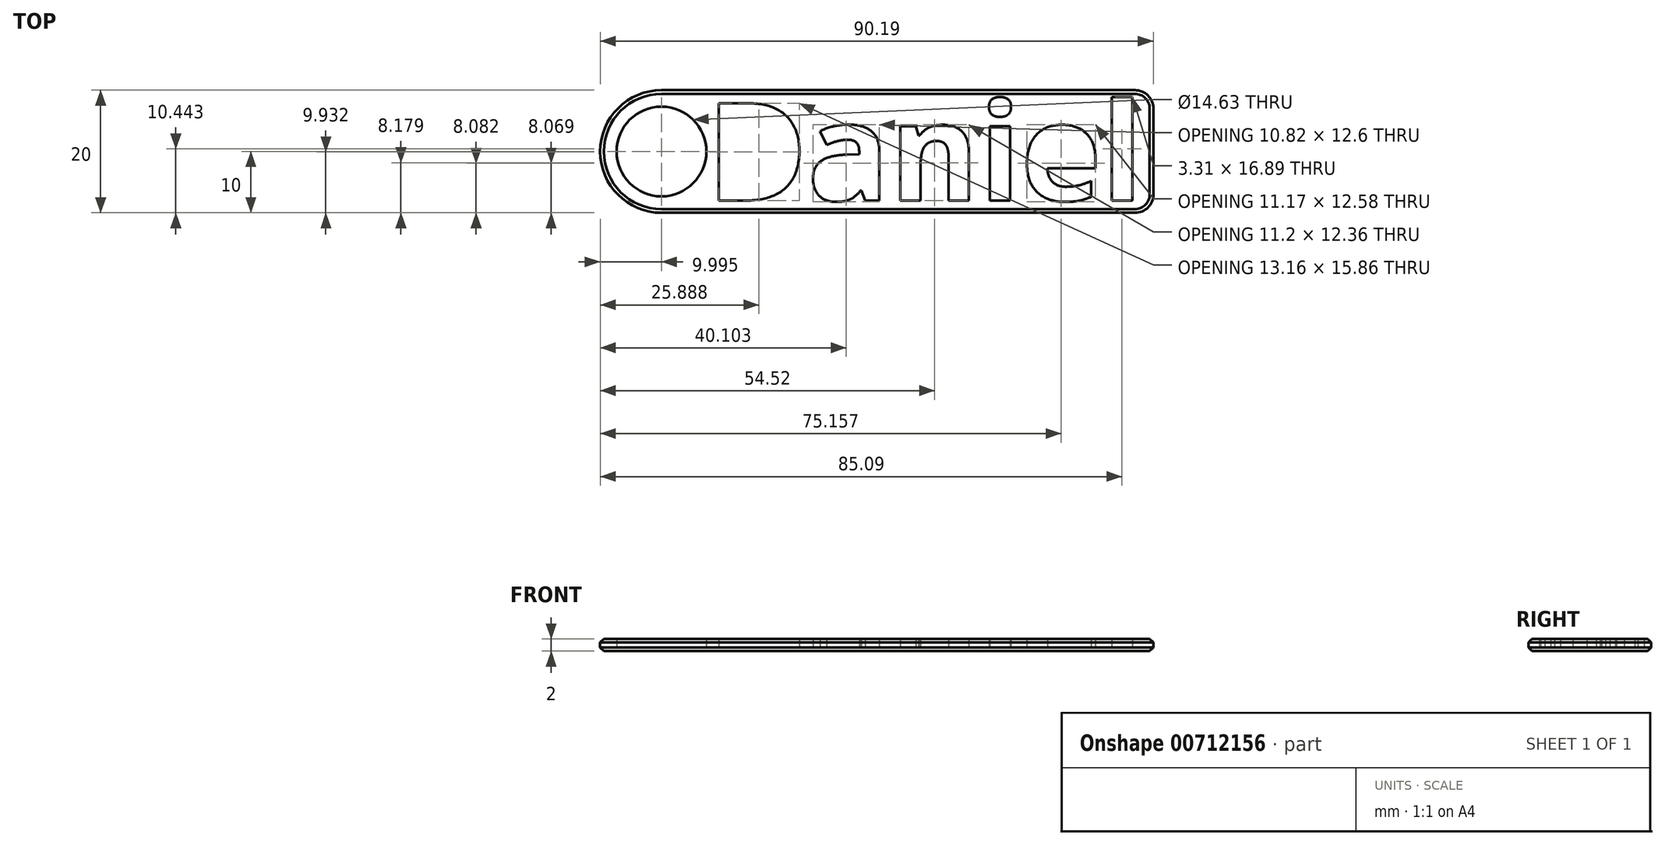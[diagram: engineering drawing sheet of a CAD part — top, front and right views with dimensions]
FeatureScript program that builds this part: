
annotation { "Feature Type Name" : "Feature", "Feature Type Description" : "" }
export const myFeature = defineFeature(function(context is Context, id is Id, definition is map)
    precondition{}
    {
        {
            var Q0;
            Q0=qCreatedBy(makeId("Top.planeOp"),FACE);
            var sketch = newSketch(context, id + "F0", { "sketchPlane" : qUnion([Q0])});
            skCircle(sketch, "E0", {"center": v(-36.96, 0) * mm, "radius": 7.32 * mm});
            skLineSegment(sketch, "E1", {"start": v(-36.96, 0) * mm, "end": v(-36.96, 10) * mm, "construction": true});
            skLineSegment(sketch, "E2", {"start": v(-36.96, 0) * mm, "end": v(-36.96, -10) * mm, "construction": true});
            skArc(sketch, "E3", {"start": v(-36.96, 10) * mm, "mid": v(-46.96, 0) * mm, "end": v(-36.96, -10) * mm});
            skLineSegment(sketch, "E4", {"start": v(-36.96, 10) * mm, "end": v(40.23, 10) * mm});
            skLineSegment(sketch, "E5", {"start": v(43.23, 7) * mm, "end": v(43.23, -7) * mm});
            skLineSegment(sketch, "E6", {"start": v(40.23, -10) * mm, "end": v(-36.96, -10) * mm});
            skText(sketch, "E7", { "text": "Daniel", "fontName": "OpenSans-Bold.ttf"});
            skLineSegment(sketch, "E8", {"start": v(-29.65, 8) * mm, "end": v(-29.65, 10) * mm, "construction": true});
            skLineSegment(sketch, "E9", {"start": v(41.23, 8) * mm, "end": v(43.23, 8) * mm, "construction": true});
            skLineSegment(sketch, "E10", {"start": v(-29.65, -8) * mm, "end": v(-29.65, -10) * mm, "construction": true});
            skPoint(sketch, "E11.visualSharp", {"position": v(43.23, 10) * mm});
            skArc(sketch, "E11.filletArc", {"start": v(43.23, 7) * mm, "mid": v(42.35, 9.12) * mm, "end": v(40.23, 10) * mm});
            skPoint(sketch, "E12.visualSharp", {"position": v(43.23, -10) * mm});
            skArc(sketch, "E12.filletArc", {"start": v(40.23, -10) * mm, "mid": v(42.35, -9.12) * mm, "end": v(43.23, -7) * mm});
            const initialGuessF0  = {"E7": [-0.02965, -0.008, 1, 0, 0.016]};
            skSetInitialGuess(sketch, initialGuessF0);
            skSolve(sketch);
        }
        {
            var Q0;
            Q0=makeQuery(id+"F0.imprint","IMPRINT",FACE,{"disambiguationData":[TD([[makeQuery(id+"F0.imprint","IMPRINT",EDGE,{"derivedFrom":sQuery(id+"F0.wireOp",EDGE,"E0")}),-1.0]])]});
            extrude(context, id + "F1", {"entities" : qUnion([Q0]), "depth" : 2 * mm, "offsetDistance" : 25 * mm});
        }
        {
            var Q0;
            Q0=makeQuery(id+"F1.opExtrude","CAP_EDGE",EDGE,{"disambiguationData":[OSD([sQuery(id+"F0.wireOp",EDGE,"E4")])],"isStart":false});
            var Q1;
            Q1=makeQuery(id+"F1.opExtrude","CAP_EDGE",EDGE,{"disambiguationData":[OSD([sQuery(id+"F0.wireOp",EDGE,"E4")])],"isStart":true});
            chamfer(context, id + "F2", {"entities" : qUnion([Q0, Q1]), "width" : 0.6 * mm, "tangentPropagation" : true});
        }
    });
